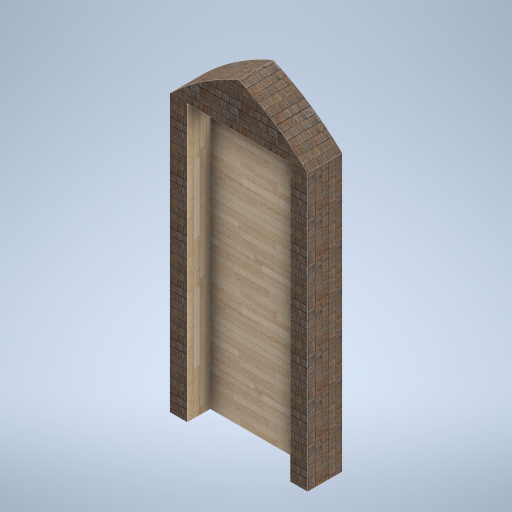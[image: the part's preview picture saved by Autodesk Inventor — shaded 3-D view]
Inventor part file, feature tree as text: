
AUTODESK INVENTOR PART (.ipt)
format: ipt  version: 2024.2 (Build 282272000, 272)  size: 470,528 bytes
history: native  units: mm
features: sketch x7, extrude x5, other x2
ambient origin geometry x8: Origin, YZ Plane, XZ Plane, XY Plane, X Axis, Y Axis, Z Axis, Center Point
bodies: Solid1 (feature_tree)
feature tree (14):
  extrude  "Extrusion1"  Depth=2000.0mm
  extrude  "Extrusion2"  TaperAngle=0.0deg  [1 undecoded]
  extrude  "擠出3"  Depth=300.0mm TaperAngle=0.0deg
  other  "刪除面1"
  sketch  "草圖4"
  sketch  "草圖5"
  sketch  "草圖6"
  extrude  "擠出4"  Depth=150.0mm
  extrude  "擠出5"  Depth=150.0mm
  other  "螺紋1"
  sketch  "Sketch1"  dims[d0=300.0mm d1=0.0mm d8=2000.0mm]
  sketch  "Sketch2"  dims[d9=2000.0mm d10=0.0mm d11=0.0mm d12=300.0mm d13=0.0mm d14=150.0mm d15=150.0mm d16=200.0mm d17=0.0mm d18=100.0mm d19=50.0mm d20=0.0mm d21=20.0mm d22=0.0mm d6=500.0mm d7=0.872665mm]
  sketch  "草圖3"
  sketch  "草圖7"
note: 1 required parameter value undecoded (feature->parameter linkage not recoverable at this tier; creation-order binding heuristic only, values carry confidence <= 0.55)
